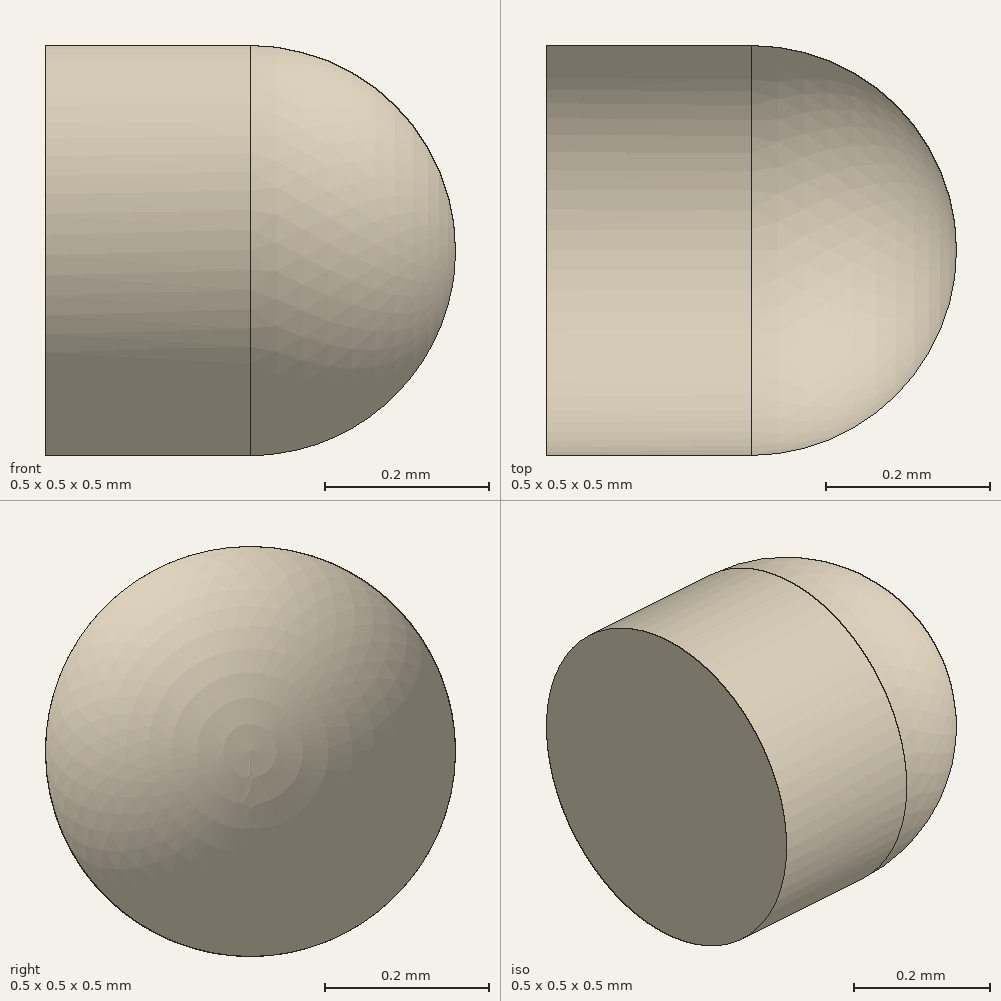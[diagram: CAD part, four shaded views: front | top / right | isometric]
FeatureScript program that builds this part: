
annotation { "Feature Type Name" : "Feature", "Feature Type Description" : "" }
export const myFeature = defineFeature(function(context is Context, id is Id, definition is map)
    precondition{}
    {
        {
            var Q0;
            Q0=qCreatedBy(makeId("Front.planeOp"),FACE);
            var sketch = newSketch(context, id + "F0", { "sketchPlane" : qUnion([Q0])});
            skLineSegment(sketch, "E0", {"start": v(0, 0) * mm, "end": v(-0.25, 0) * mm});
            skLineSegment(sketch, "E1", {"start": v(-0.25, 0) * mm, "end": v(-0.25, 0.25) * mm});
            skLineSegment(sketch, "E2", {"start": v(-0.25, 0.25) * mm, "end": v(0.25, 0.25) * mm});
            skArc(sketch, "E3", {"start": v(0, 0) * mm, "mid": v(0.18, 0.07) * mm, "end": v(0.25, 0.25) * mm});
            skSolve(sketch);
        }
        {
            var Q0;
            Q0 = qSketchRegion(id + "F0", true);
            var Q1;
            Q1=sQuery(id+"F0.wireOp",EDGE,"E2");
            revolve(context, id + "F1", {"entities" : qUnion([Q0]), "axis" : qUnion([Q1]), "revolveType" : RevolveType.FULL});
        }
    });
